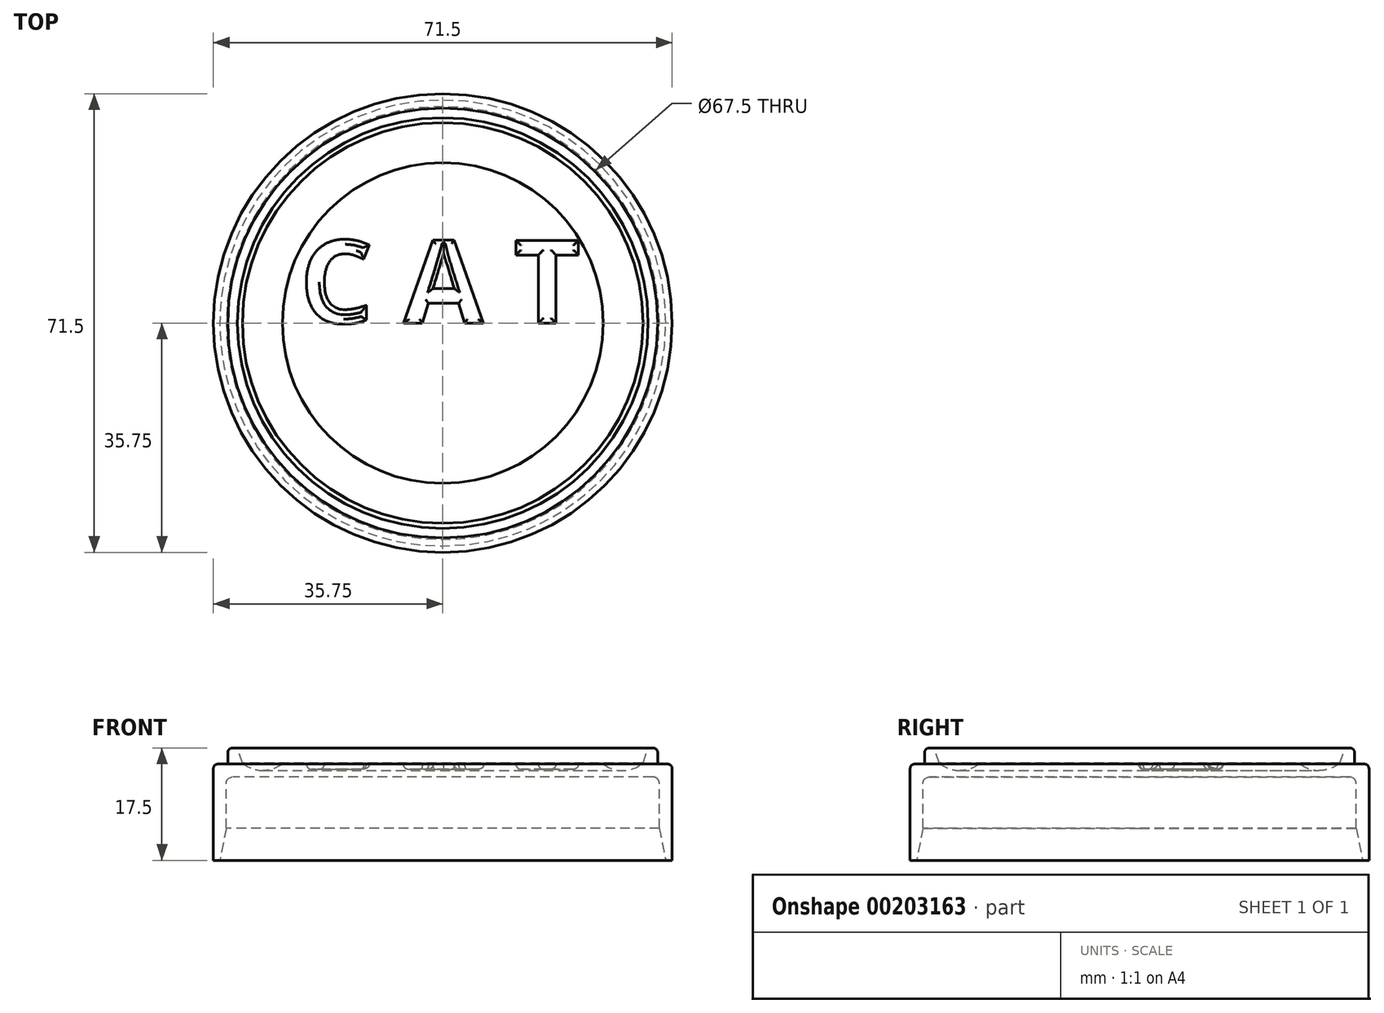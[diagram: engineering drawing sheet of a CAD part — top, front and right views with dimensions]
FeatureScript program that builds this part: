
annotation { "Feature Type Name" : "Feature", "Feature Type Description" : "" }
export const myFeature = defineFeature(function(context is Context, id is Id, definition is map)
    precondition{}
    {
        {
            var Q0;
            Q0=qCreatedBy(makeId("Top.planeOp"),FACE);
            var sketch = newSketch(context, id + "F0", { "sketchPlane" : qUnion([Q0])});
            skCircle(sketch, "E0", {"center": v(0, 0) * mm, "radius": 33.75 * mm});
            skCircle(sketch, "E1", {"center": v(0, 0) * mm, "radius": 35.75 * mm});
            skText(sketch, "E2", { "text": "C A T", "fontName": "OpenSans-Bold.ttf"});
            const initialGuessF0  = {"E2": [-0.0223, 0, 1, 0, 0.013]};
            skSetInitialGuess(sketch, initialGuessF0);
            skSolve(sketch);
        }
        {
            var Q0;
            Q0=qSketchRegion(id+"F0",true);
            var Q1;
            Q1=makeQuery(id+"F0.imprint","IMPRINT",FACE,{"disambiguationData":[TD([[makeQuery(id+"F0.imprint","IMPRINT",EDGE,{"derivedFrom":sQuery(id+"F0.wireOp",EDGE,"E0")}),-1.0]])]});
            extrude(context, id + "F1", {"entities" : qUnion([Q0, Q1]), "oppositeDirection" : true, "depth" : 15 * mm});
        }
        {
            var Q0;
            Q0=makeQuery(id+"F0.imprint","IMPRINT",FACE,{"disambiguationData":[TD([[makeQuery(id+"F0.imprint","IMPRINT",EDGE,{"derivedFrom":sQuery(id+"F0.wireOp",EDGE,"E0")}),1.0]])]});
            var Q1;
            Q1=qSketchRegion(id+"F0",true);
            var Q2;
            Q2=makeQuery(id+"F0.imprint","IMPRINT",FACE,{"disambiguationData":[TD([[makeQuery(id+"F0.imprint","IMPRINT",EDGE,{"derivedFrom":sQuery(id+"F0.wireOp",EDGE,"E2.sketch_text.stroke-15")}),-1.0]])]});
            var Q3;
            Q3=makeQuery(id+"F0.imprint","IMPRINT",FACE,{"disambiguationData":[TD([[makeQuery(id+"F0.imprint","IMPRINT",EDGE,{"derivedFrom":sQuery(id+"F0.wireOp",EDGE,"E2.sketch_text.stroke-27")}),-1.0]])]});
            var Q4;
            Q4=makeQuery(id+"F0.imprint","IMPRINT",FACE,{"disambiguationData":[TD([[makeQuery(id+"F0.imprint","IMPRINT",EDGE,{"derivedFrom":sQuery(id+"F0.wireOp",EDGE,"E2.sketch_text.stroke-23")}),1.0]])]});
            var Q5;
            Q5=makeQuery(id+"F0.imprint","IMPRINT",FACE,{"disambiguationData":[TD([[makeQuery(id+"F0.imprint","IMPRINT",EDGE,{"derivedFrom":sQuery(id+"F0.wireOp",EDGE,"E2.sketch_text.stroke-0")}),-1.0]])]});
            extrude(context, id + "F2", {"entities" : qUnion([Q0, Q1, Q2, Q3, Q4, Q5]), "operationType" : NewBodyOperationType.ADD, "oppositeDirection" : true, "depth" : 2 * mm});
        }
        {
            var Q0;
            Q0=makeQuery(id+"F0.imprint","IMPRINT",FACE,{"disambiguationData":[TD([[makeQuery(id+"F0.imprint","IMPRINT",EDGE,{"derivedFrom":sQuery(id+"F0.wireOp",EDGE,"E2.sketch_text.stroke-15")}),-1.0]])]});
            var Q1;
            Q1=makeQuery(id+"F0.imprint","IMPRINT",FACE,{"disambiguationData":[TD([[makeQuery(id+"F0.imprint","IMPRINT",EDGE,{"derivedFrom":sQuery(id+"F0.wireOp",EDGE,"E2.sketch_text.stroke-27")}),-1.0]])]});
            var Q2;
            Q2=makeQuery(id+"F0.imprint","IMPRINT",FACE,{"disambiguationData":[TD([[makeQuery(id+"F0.imprint","IMPRINT",EDGE,{"derivedFrom":sQuery(id+"F0.wireOp",EDGE,"E2.sketch_text.stroke-0")}),-1.0]])]});
            extrude(context, id + "F3", {"entities" : qUnion([Q0, Q1, Q2]), "operationType" : NewBodyOperationType.REMOVE, "oppositeDirection" : true, "depth" : .8 * mm});
        }
        {
            var Q0;
            Q0=makeQuery(id+"F2.opExtrude","CAP_FACE",FACE,{"disambiguationData":[OSD([sQuery(id+"F0.wireOp",EDGE,"E1")])],"isStart":false});
            fillet(context, id + "F4", {"entities" : qUnion([Q0]), "radius" : 1 * mm, "tangentPropagation" : true, "allowEdgeOverflow" : false});
        }
        {
            var Q0;
            Q0=makeQuery(id+"F1.opExtrude","CAP_EDGE",EDGE,{"disambiguationData":[OSD([sQuery(id+"F0.wireOp",EDGE,"E0")])],"isStart":false});
            chamfer(context, id + "F5", {"entities" : qUnion([Q0]), "chamferType" : ChamferType.TWO_OFFSETS, "width1" : 1 * mm, "oppositeDirection" : false, "width2" : 5 * mm, "tangentPropagation" : true});
        }
        {
            var Q0;
            Q0=qCreatedBy(makeId("Front.planeOp"),FACE);
            var sketch = newSketch(context, id + "F6", { "sketchPlane" : qUnion([Q0])});
            skLineSegment(sketch, "E3", {"start": v(35.75, -1) * mm, "end": v(35.75, -15) * mm});
            skLineSegment(sketch, "E4", {"start": v(-35.75, -15) * mm, "end": v(-35.75, -1) * mm});
            skLineSegment(sketch, "E5", {"start": v(0, -0.6) * mm, "end": v(0, 0) * mm});
            skLineSegment(sketch, "E6", {"start": v(35.75, 0) * mm, "end": v(35.75, -15) * mm});
            skLineSegment(sketch, "E7", {"start": v(-35.75, -15) * mm, "end": v(-35.75, 0) * mm});
            skLineSegment(sketch, "E8.0", {"start": v(-35.75, -15) * mm, "end": v(35.75, -15) * mm});
            skArc(sketch, "E9", {"start": v(-31, 0) * mm, "mid": v(-28, -1) * mm, "end": v(-25, 0) * mm});
            skLineSegment(sketch, "E10", {"start": v(-31, 0) * mm, "end": v(0, 0) * mm});
            skSolve(sketch);
        }
        {
            var Q0;
            {var subQ0=sQuery(id+"F6.wireOp",EDGE,"E10");var subQ1=sQuery(id+"F6.wireOp",EDGE,"E9");var subQ2=makeQuery(id+"F6.imprint","INTERSECT",VERTEX,{"disambiguationData":[OD(0.0)],"derivedFrom":[subQ1,subQ0]});Q0=makeQuery(id+"F6.imprint","IMPRINT",FACE,{"disambiguationData":[TD([[makeQuery(id+"F6.imprint","IMPRINT",EDGE,{"disambiguationData":[TD([[subQ2,-1.0]])],"derivedFrom":subQ1}),1.0]])]});}
            var Q1;
            {var subQ0=sQuery(id+"F6.wireOp",EDGE,"E5");Q1=makeQuery(id+"F6.imprint","IMPRINT",FACE,{"disambiguationData":[TD([[makeQuery(id+"F6.imprint","IMPRINT",EDGE,{"derivedFrom":subQ0}),1.0]])]});}
            var Q2;
            {var subQ0=makeQuery(id+"F2.opExtrude","CAP_FACE",FACE,{"disambiguationData":[OSD([sQuery(id+"F0.wireOp",EDGE,"E1")])],"isStart":false});Q2=makeQuery(id+"F4.opFillet","BLEND_EDGE",EDGE,{"blendedFrom":[makeQuery(id+"F2.boolean.opBoolean","INTERSECT",EDGE,{"derivedFrom":[makeQuery(id+"F1.opExtrude","SWEPT_FACE",FACE,{"disambiguationData":[OSD([sQuery(id+"F0.wireOp",EDGE,"E0")])]}),subQ0]}),subQ0],"blendedInto":[subQ0]});}
            revolve(context, id + "F7", {"operationType" : NewBodyOperationType.REMOVE, "entities" : qUnion([Q0, Q1]), "axis" : qUnion([Q2]), "revolveType" : RevolveType.FULL, "oppositeDirection" : true});
        }
        {
            var Q0;
            {var subQ0=sQuery(id+"F0.wireOp",EDGE,"E1");var subQ1=makeQuery(id+"F1.opExtrude","SWEPT_FACE",FACE,{"disambiguationData":[OSD([subQ0])]});Q0=makeQuery(id+"F7.boolean.opBoolean","SPLIT",FACE,{"disambiguationData":[TD([subQ1])],"derivedFrom":makeQuery(id+"F3.boolean.opBoolean","SPLIT",FACE,{"disambiguationData":[TD([subQ1])],"derivedFrom":makeQuery(id+"F2.boolean.opBoolean","MERGE",FACE,{"derivedFrom":[makeQuery(id+"F1.opExtrude","CAP_FACE",FACE,{"disambiguationData":[OSD([sQuery(id+"F0.wireOp",EDGE,"E0"),subQ0])],"isStart":true}),makeQuery(id+"F2.opExtrude","CAP_FACE",FACE,{"disambiguationData":[OSD([subQ0])],"isStart":true})]})})});}
            var sketch = newSketch(context, id + "F8", { "sketchPlane" : qUnion([Q0])});
            skCircle(sketch, "E11.0.0", {"center": v(0, 0) * mm, "radius": 35.75 * mm});
            skCircle(sketch, "E12.0", {"center": v(0, 0) * mm, "radius": 31 * mm});
            skCircle(sketch, "E13", {"center": v(0, 0) * mm, "radius": 33.5 * mm});
            skSolve(sketch);
        }
        {
            var Q0;
            Q0=makeQuery(id+"F8.imprint","IMPRINT",FACE,{"disambiguationData":[TD([[makeQuery(id+"F8.imprint","IMPRINT",EDGE,{"derivedFrom":sQuery(id+"F8.wireOp",EDGE,"E12.0")}),-1.0]])]});
            extrude(context, id + "F9", {"entities" : qUnion([Q0]), "operationType" : NewBodyOperationType.ADD, "depth" : 2.5 * mm});
        }
        {
            var Q0;
            Q0=makeQuery(id+"F9.opExtrude","CAP_EDGE",EDGE,{"disambiguationData":[OSD([sQuery(id+"F8.wireOp",EDGE,"E13")])],"isStart":true});
            var Q1;
            Q1=makeQuery(id+"F1.opExtrude","CAP_EDGE",EDGE,{"disambiguationData":[OSD([sQuery(id+"F0.wireOp",EDGE,"E1")])],"isStart":true});
            var Q2;
            Q2=makeQuery(id+"F9.opExtrude","CAP_EDGE",EDGE,{"disambiguationData":[OSD([sQuery(id+"F8.wireOp",EDGE,"E13")])],"isStart":false});
            fillet(context, id + "F10", {"entities" : qUnion([Q0, Q1, Q2]), "radius" : .7 * mm, "tangentPropagation" : true, "allowEdgeOverflow" : false});
        }
        {
            var Q0;
            Q0=makeQuery(id+"F3.boolean.opBoolean","COPY",FACE,{"derivedFrom":makeQuery(id+"F3.opExtrude","CAP_FACE",FACE,{"disambiguationData":[OSD([sQuery(id+"F0.wireOp",EDGE,"E2.sketch_text.stroke-0"),sQuery(id+"F0.wireOp",EDGE,"E2.sketch_text.stroke-1"),sQuery(id+"F0.wireOp",EDGE,"E2.sketch_text.stroke-2"),sQuery(id+"F0.wireOp",EDGE,"E2.sketch_text.stroke-3"),sQuery(id+"F0.wireOp",EDGE,"E2.sketch_text.stroke-4"),sQuery(id+"F0.wireOp",EDGE,"E2.sketch_text.stroke-5"),sQuery(id+"F0.wireOp",EDGE,"E2.sketch_text.stroke-6"),sQuery(id+"F0.wireOp",EDGE,"E2.sketch_text.stroke-7"),sQuery(id+"F0.wireOp",EDGE,"E2.sketch_text.stroke-8"),sQuery(id+"F0.wireOp",EDGE,"E2.sketch_text.stroke-9"),sQuery(id+"F0.wireOp",EDGE,"E2.sketch_text.stroke-10"),sQuery(id+"F0.wireOp",EDGE,"E2.sketch_text.stroke-11"),sQuery(id+"F0.wireOp",EDGE,"E2.sketch_text.stroke-12"),sQuery(id+"F0.wireOp",EDGE,"E2.sketch_text.stroke-13"),sQuery(id+"F0.wireOp",EDGE,"E2.sketch_text.stroke-14")])],"isStart":false})});
            var Q1;
            Q1=makeQuery(id+"F3.boolean.opBoolean","COPY",FACE,{"derivedFrom":makeQuery(id+"F3.opExtrude","CAP_FACE",FACE,{"disambiguationData":[OSD([sQuery(id+"F0.wireOp",EDGE,"E2.sketch_text.stroke-27"),sQuery(id+"F0.wireOp",EDGE,"E2.sketch_text.stroke-28"),sQuery(id+"F0.wireOp",EDGE,"E2.sketch_text.stroke-29"),sQuery(id+"F0.wireOp",EDGE,"E2.sketch_text.stroke-30"),sQuery(id+"F0.wireOp",EDGE,"E2.sketch_text.stroke-31"),sQuery(id+"F0.wireOp",EDGE,"E2.sketch_text.stroke-32"),sQuery(id+"F0.wireOp",EDGE,"E2.sketch_text.stroke-33"),sQuery(id+"F0.wireOp",EDGE,"E2.sketch_text.stroke-34")])],"isStart":false})});
            fillet(context, id + "F11", {"entities" : qUnion([Q0, Q1]), "radius" : .8 * mm, "tangentPropagation" : true, "allowEdgeOverflow" : false});
        }
        {
            var Q0;
            Q0=makeQuery(id+"F3.boolean.opBoolean","COPY",FACE,{"derivedFrom":makeQuery(id+"F3.opExtrude","CAP_FACE",FACE,{"disambiguationData":[OSD([sQuery(id+"F0.wireOp",EDGE,"E2.sketch_text.stroke-15"),sQuery(id+"F0.wireOp",EDGE,"E2.sketch_text.stroke-16"),sQuery(id+"F0.wireOp",EDGE,"E2.sketch_text.stroke-17"),sQuery(id+"F0.wireOp",EDGE,"E2.sketch_text.stroke-18"),sQuery(id+"F0.wireOp",EDGE,"E2.sketch_text.stroke-19"),sQuery(id+"F0.wireOp",EDGE,"E2.sketch_text.stroke-20"),sQuery(id+"F0.wireOp",EDGE,"E2.sketch_text.stroke-21"),sQuery(id+"F0.wireOp",EDGE,"E2.sketch_text.stroke-22"),sQuery(id+"F0.wireOp",EDGE,"E2.sketch_text.stroke-23"),sQuery(id+"F0.wireOp",EDGE,"E2.sketch_text.stroke-24"),sQuery(id+"F0.wireOp",EDGE,"E2.sketch_text.stroke-25"),sQuery(id+"F0.wireOp",EDGE,"E2.sketch_text.stroke-26")])],"isStart":false})});
            fillet(context, id + "F12", {"entities" : qUnion([Q0]), "radius" : .6 * mm, "tangentPropagation" : true, "allowEdgeOverflow" : false});
        }
        {
            var Q0;
            Q0=makeQuery(id+"F9.opExtrude","CAP_EDGE",EDGE,{"disambiguationData":[OSD([sQuery(id+"F8.wireOp",EDGE,"E12.0")])],"isStart":false});
            chamfer(context, id + "F13", {"entities" : qUnion([Q0]), "chamferType" : ChamferType.TWO_OFFSETS, "width1" : 3 * mm, "oppositeDirection" : false, "width2" : 1 * mm, "tangentPropagation" : true});
        }
    });
